# Revit family: Фильтр К Naveka (2)
name_source: partatom
category: Арматура воздуховодов
units: mm (PartAtom-declared; Revit-internal decimal feet)

## family parameters
Всегда вертикально = Да
Заголовок OmniClass = Climate Control (HVAC)
На основе рабочей плоскости = Нет
Номер OmniClass = 23.75.00.00
Общий = Нет
При загрузке вырезать с полостями = Нет
Размер круглого соединителя = Использовать диаметр
Тип детали = Вставляется

## types (12) — shared parameters
ADSK_Единица измерения = шт.
ADSK_Завод-изготовитель = Naveka
ADSK_Примечание = https://progress-nw.ru
Материал = RAL 0000 Серый металл
zero-valued in all types: ADSK_Масса

## per-type parameters (varying)
| type | ADSK_Наименование | B | D | D+0.5 | D+4.5 | H | L | d | Прижимы 2 шт. | Прижимы 4 шт. |
| К-100 компакт | Корпус компактного фильтра круглого | 200 мм | 49 мм | 50 мм | 54 мм | 204 мм | 150 мм | 100 мм | Да | Нет |
| К-125 компакт | Корпус компактного фильтра круглого | 200 мм | 62 мм | 62 мм | 66 мм | 204 мм | 150 мм | 125 мм | Да | Нет |
| К-160 компакт | Корпус компактного фильтра круглого | 200 мм | 79 мм | 80 мм | 84 мм | 204 мм | 150 мм | 160 мм | Да | Нет |
| К-200 компакт | Корпус компактного фильтра круглого | 241 мм | 99 мм | 100 мм | 104 мм | 245 мм | 150 мм | 200 мм | Да | Нет |
| К-250 компакт | Корпус компактного фильтра круглого | 300 мм | 124 мм | 125 мм | 129 мм | 304 мм | 150 мм | 250 мм | Да | Нет |
| К-315 компакт | Корпус компактного фильтра круглого | 341 мм | 157 мм | 157 мм | 161 мм | 345 мм | 150 мм | 315 мм | Да | Нет |
| К-100 | Корпус карманного фильтра круглого | 200 мм | 49 мм | 50 мм | 54 мм | 204 мм | 402 мм | 100 мм | Нет | Да |
| К-125 | Корпус карманного фильтра круглого | 200 мм | 62 мм | 62 мм | 66 мм | 204 мм | 402 мм | 125 мм | Нет | Да |
| К-160 | Корпус карманного фильтра круглого | 200 мм | 79 мм | 80 мм | 84 мм | 204 мм | 402 мм | 160 мм | Нет | Да |
| К-200 | Корпус карманного фильтра круглого | 241 мм | 99 мм | 100 мм | 104 мм | 245 мм | 408 мм | 200 мм | Нет | Да |
| К-250 | Корпус карманного фильтра круглого | 300 мм | 124 мм | 125 мм | 129 мм | 304 мм | 468 мм | 250 мм | Нет | Да |
| К-315 | Корпус карманного фильтра круглого | 341 мм | 157 мм | 157 мм | 161 мм | 345 мм | 518 мм | 315 мм | Нет | Да |

note: column(s) folded — value = type name in every type: ADSK_Марка
